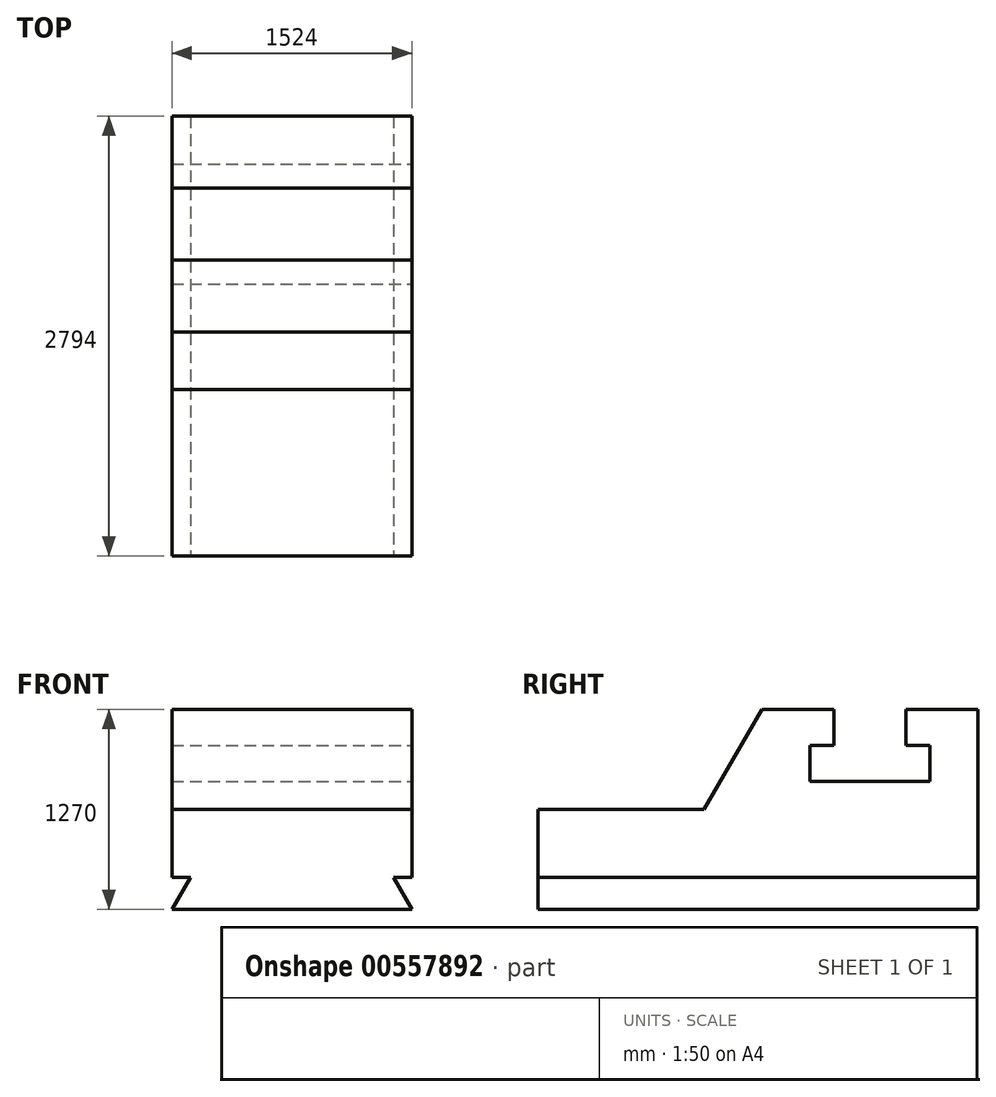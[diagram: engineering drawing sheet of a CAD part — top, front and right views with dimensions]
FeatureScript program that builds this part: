
annotation { "Feature Type Name" : "Feature", "Feature Type Description" : "" }
export const myFeature = defineFeature(function(context is Context, id is Id, definition is map)
    precondition{}
    {
        {
            var Q0;
            Q0=qCreatedBy(makeId("Right.planeOp"),FACE);
            var sketch = newSketch(context, id + "F0", { "sketchPlane" : qUnion([Q0])});
            skLineSegment(sketch, "E0", {"start": v(-102.82, -57.28) * mm, "end": v(2691.18, -57.28) * mm});
            skLineSegment(sketch, "E1", {"start": v(2691.18, -57.28) * mm, "end": v(2691.18, 1212.72) * mm});
            skLineSegment(sketch, "E2", {"start": v(2691.18, 1212.72) * mm, "end": v(2233.98, 1212.72) * mm});
            skLineSegment(sketch, "E3", {"start": v(2233.98, 1212.72) * mm, "end": v(2233.98, 984.12) * mm});
            skLineSegment(sketch, "E4", {"start": v(2233.98, 984.12) * mm, "end": v(2386.38, 984.12) * mm});
            skLineSegment(sketch, "E5", {"start": v(2386.38, 984.12) * mm, "end": v(2386.38, 755.52) * mm});
            skLineSegment(sketch, "E6", {"start": v(2386.38, 755.52) * mm, "end": v(1624.38, 755.52) * mm});
            skLineSegment(sketch, "E7", {"start": v(1624.38, 755.52) * mm, "end": v(1624.38, 984.12) * mm});
            skLineSegment(sketch, "E8", {"start": v(1624.38, 984.12) * mm, "end": v(1776.78, 984.12) * mm});
            skLineSegment(sketch, "E9", {"start": v(1776.78, 984.12) * mm, "end": v(1776.78, 1212.72) * mm});
            skLineSegment(sketch, "E10", {"start": v(1776.78, 1212.72) * mm, "end": v(1319.58, 1212.72) * mm});
            skLineSegment(sketch, "E11", {"start": v(-102.82, -57.28) * mm, "end": v(-102.82, 577.72) * mm});
            skLineSegment(sketch, "E12", {"start": v(1319.58, 1212.72) * mm, "end": v(952.96, 577.72) * mm});
            skLineSegment(sketch, "E13", {"start": v(952.96, 577.72) * mm, "end": v(-102.82, 577.72) * mm});
            skSolve(sketch);
        }
        {
            var Q0;
            Q0=makeQuery(id+"F0.imprint","IMPRINT",FACE,{"disambiguationData":[TD([[makeQuery(id+"F0.imprint","IMPRINT",EDGE,{"derivedFrom":sQuery(id+"F0.wireOp",EDGE,"E0")}),1.0]])]});
            extrude(context, id + "F1", {"entities" : qUnion([Q0]), "oppositeDirection" : true, "depth" : 1524 * mm, "offsetDistance" : 25.4 * mm});
        }
        {
            var Q0;
            Q0=makeQuery(id+"F1.opExtrude","SWEPT_FACE",FACE,{"disambiguationData":[OSD([sQuery(id+"F0.wireOp",EDGE,"E11")])]});
            var sketch = newSketch(context, id + "F2", { "sketchPlane" : qUnion([Q0])});
            skLineSegment(sketch, "E14", {"start": v(0, 145.92) * mm, "end": v(-117.32, 145.92) * mm});
            skLineSegment(sketch, "E15", {"start": v(-117.32, 145.92) * mm, "end": v(0, -57.28) * mm});
            skSolve(sketch);
        }
        {
            var Q0;
            {var subQ0=sQuery(id+"F2.wireOp",EDGE,"E14");Q0=makeQuery(id+"F2.imprint","IMPRINT",FACE,{"disambiguationData":[TD([[makeQuery(id+"F2.imprint","IMPRINT",EDGE,{"derivedFrom":subQ0}),1.0]])]});}
            extrude(context, id + "F3", {"entities" : qUnion([Q0]), "operationType" : NewBodyOperationType.REMOVE, "endBound" : BoundingType.THROUGH_ALL, "oppositeDirection" : true, "depth" : 25.4 * mm, "offsetDistance" : 25.4 * mm});
        }
        {
            var Q0;
            Q0=makeQuery(id+"F1.opExtrude","SWEPT_FACE",FACE,{"disambiguationData":[OSD([sQuery(id+"F0.wireOp",EDGE,"E11")])]});
            var sketch = newSketch(context, id + "F4", { "sketchPlane" : qUnion([Q0])});
            skLineSegment(sketch, "E16", {"start": v(-1524, -57.28) * mm, "end": v(-1406.68, 145.92) * mm});
            skLineSegment(sketch, "E17", {"start": v(-1406.68, 145.92) * mm, "end": v(-1524, 145.92) * mm});
            skSolve(sketch);
        }
        {
            var Q0;
            {var subQ0=sQuery(id+"F4.wireOp",EDGE,"E16");Q0=makeQuery(id+"F4.imprint","IMPRINT",FACE,{"disambiguationData":[TD([[makeQuery(id+"F4.imprint","IMPRINT",EDGE,{"derivedFrom":subQ0}),1.0]])]});}
            extrude(context, id + "F5", {"entities" : qUnion([Q0]), "operationType" : NewBodyOperationType.REMOVE, "endBound" : BoundingType.THROUGH_ALL, "oppositeDirection" : true, "depth" : 25.4 * mm, "offsetDistance" : 25.4 * mm});
        }
    });
